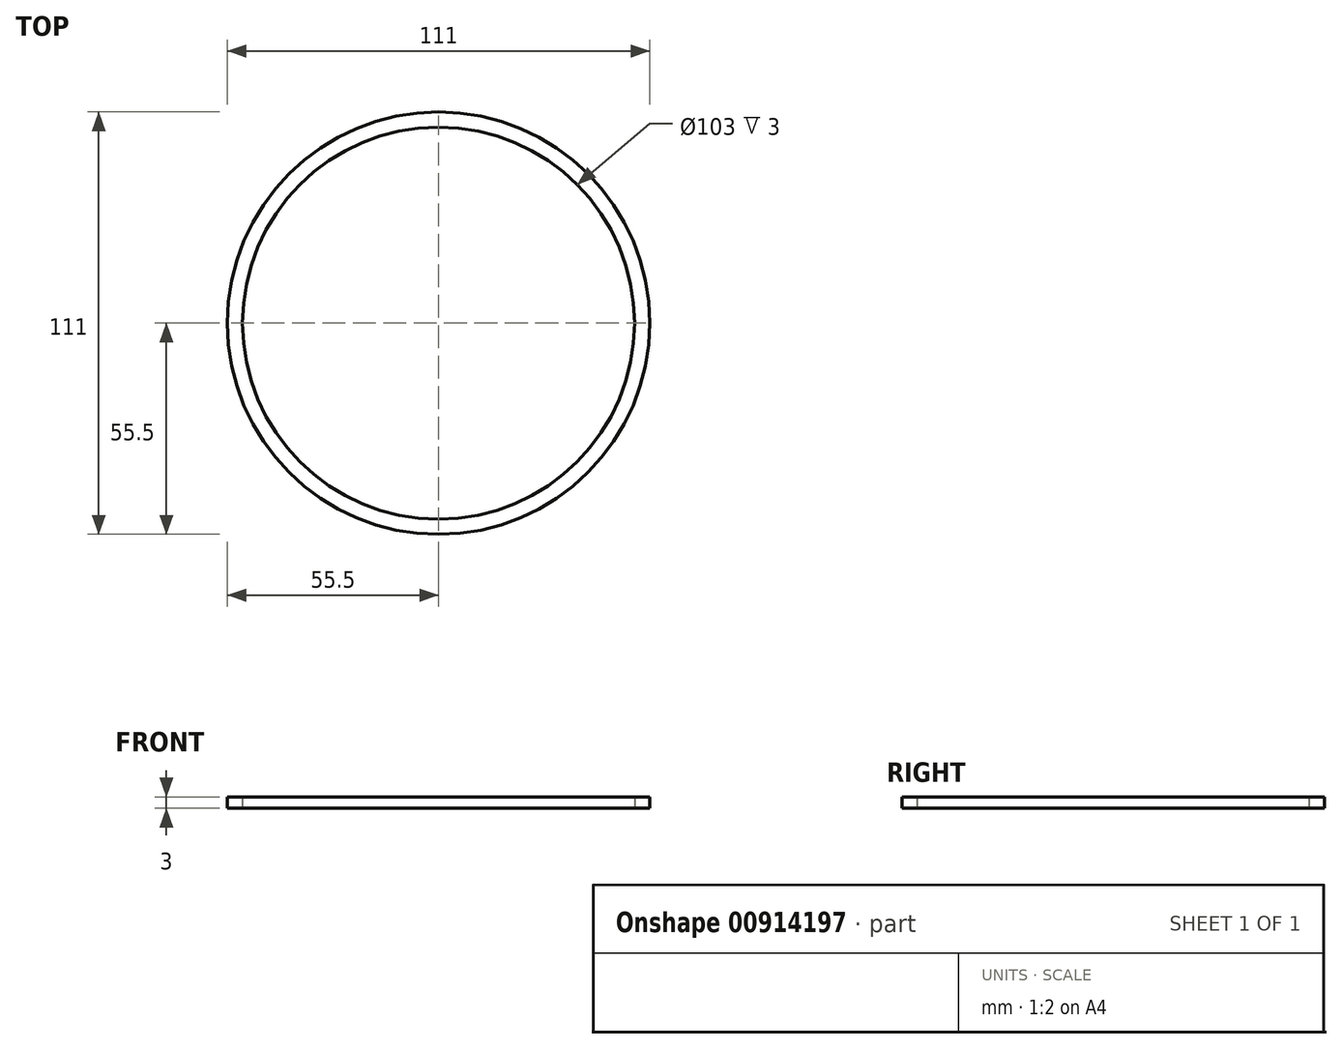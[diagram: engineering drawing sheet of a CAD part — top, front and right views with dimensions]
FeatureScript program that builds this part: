
annotation { "Feature Type Name" : "Feature", "Feature Type Description" : "" }
export const myFeature = defineFeature(function(context is Context, id is Id, definition is map)
    precondition{}
    {
        {
            var Q0;
            Q0=qCreatedBy(makeId("Top.planeOp"),FACE);
            var sketch = newSketch(context, id + "F0", { "sketchPlane" : qUnion([Q0])});
            skCircle(sketch, "E0", {"center": v(0, 0) * mm, "radius": 51.5 * mm});
            skCircle(sketch, "E1", {"center": v(0, 0) * mm, "radius": 55.5 * mm});
            skSolve(sketch);
        }
        {
            var Q0;
            Q0 = qSketchRegion(id + "F0", true);
            extrude(context, id + "F1", {"entities" : qUnion([Q0]), "depth" : 3 * mm, "offsetDistance" : 25 * mm});
        }
    });
